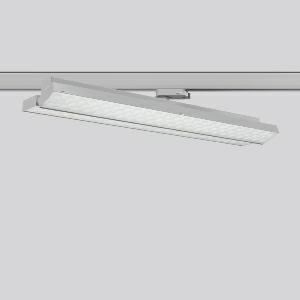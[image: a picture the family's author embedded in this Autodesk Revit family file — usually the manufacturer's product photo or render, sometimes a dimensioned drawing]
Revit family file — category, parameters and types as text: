
# Revit family: tx-move_742161_004_3_2824
name_source: partatom
category: Lighting Fixtures
units: mm (PartAtom-declared; Revit-internal decimal feet)

## family parameters
Cut with Voids When Loaded = No
Host = Face
Light Source = No
Part Type = Normal
Room Calculation Point = No
Round Connector Dimension = Use Diameter
Shared = No

## types (1)
- MultiLumen 1 (1 x LED Modul 835, 3025 lm, 3500)
    Apparent Load = 41 VA
    CIE Flux Codes = 88 96 99 100 100
    Color Rendering = 80
    Color Temperature = 3500
    Default Elevation = 1800 mm
    Description = Series: TX-MOVE
Multifunctional surface-mounted spotlight for area lighting. Very flat design. Housing: sheet steel, powder-coated. Rotation range: 356°. Swivel range: 90°. Consistent alignment possible with visible tilt scale. High-efficiency LED units with optimum light control thanks to clear plastic (PC) lens optics. Spezielle Mikrostrukturen reduzieren Gelbsaum. Symmetrical light distribution. With multi adaptor for 3-circuit tracks 230 V. Suitable for Track on ceiling. MultiLumen: Luminous flux adjustable in 3 steps. Factory setting is the highest luminous flux. Environmentally friendly and resource-saving due to replaceable and recyclable components. 
Colour: silver, matt (approx. RAL 9006)
Length: 570 mm
Width: 119 mm
Height: 92 mm
Lamp: LED
Socket: without socket
Colour temperature: 3500K
Colour rendering index (CRI): 80
System power: 41 W
Rated luminous flux: 6050 lm
Luminous efficiency: 148 lm/W
System power 2: 57 W
Rated luminous flux 2: 8200 lm
Luminous efficiency 2: 144 lm/W
System power 3: 73 W
Rated luminous flux 3: 10000 lm
Luminous efficiency 3: 137 lm/W
Control gear: Regulated power supply
Protection class: I
Type of protection: IP 20
    Height = 75 mm
    Lamp = 1 x LED Modul 835
    Lamp Light Flux = 3025 lm
    Lamp count = 1
    Length = 569 mm
    Lifetime = 50000 h
    Luminous efficacy = 148 lm/W
    Manufacturer = RZB
    ModVariant = No
    Model = 742161.004.3
    Mounting Place = Ceiling
    Mounting Type = Rail mounted
    Number of Poles = 1
    OnlyDefault = Yes
    Power Factor = 1
    Product Name = TX-MOVE
    Product group = Track mounted projectors
    ProductGroupID = 301
    Protection Class = Protection class I
    Protection Degree = IP 20
    RLX_Detail_Level = 1
    RLX_Emergency_Light_Flux = 0 lm
    RLX_Emergency_Type = 0
    RLX_Emergency_Type_DB = No
    RlxData = <blob elided: 33249 chars, md5=de2e9a83>
    Socket = socket
    Standby Power = 0 W
    System Light Flux = 6050 lm
    System Power = 41 W
    Type Comments = MultiLumen 1
    Type Image = 742162.004.jpg
    URL = http://relux.com
    VarID = multilumen_1
    Voltage = 230 V
    Voltage Range = 220-240 V
    Weight = 0.00 kg
    Width = 119 mm

## geometry (parser evidence)
native form markers: Blend x4, Sweep x13
no freeform markers — native parametric forms only
